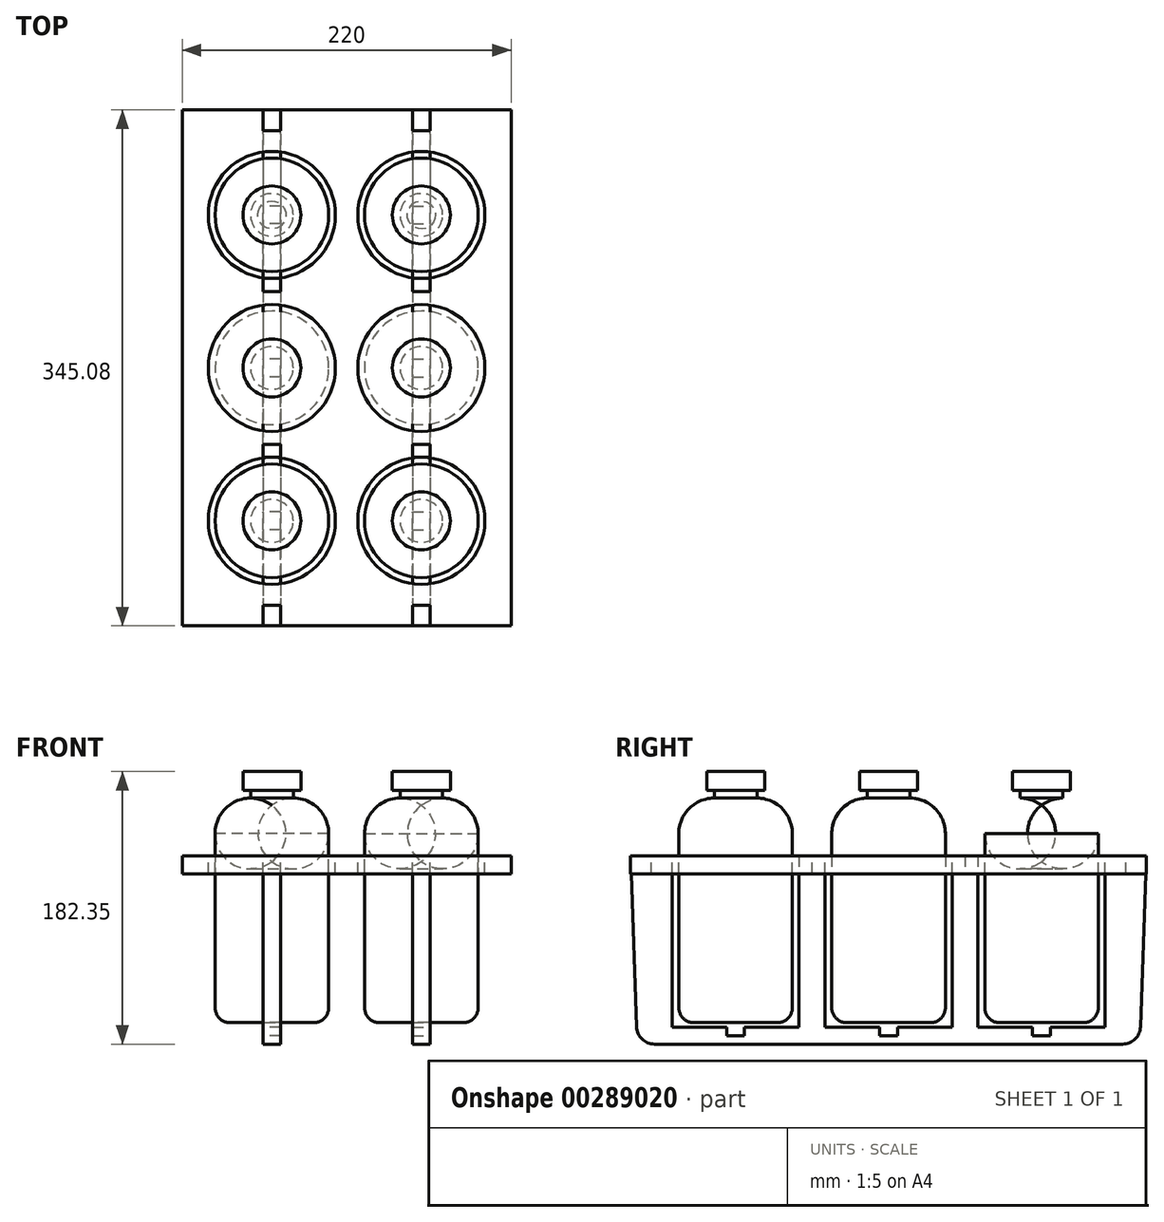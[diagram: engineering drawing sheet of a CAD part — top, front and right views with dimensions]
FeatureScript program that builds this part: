
annotation { "Feature Type Name" : "Feature", "Feature Type Description" : "" }
export const myFeature = defineFeature(function(context is Context, id is Id, definition is map)
    precondition{}
    {
        {
            var Q0;
            Q0=qCreatedBy(makeId("Right.planeOp"),FACE);
            var sketch = newSketch(context, id + "F0", { "sketchPlane" : qUnion([Q0])});
            skLineSegment(sketch, "E0", {"start": v(0, 0) * mm, "end": v(-156.67, 0) * mm});
            skLineSegment(sketch, "E1", {"start": v(-156.67, 0) * mm, "end": v(-172, 0) * mm, "construction": true});
            skLineSegment(sketch, "E2", {"start": v(-172, 0) * mm, "end": v(-172.54, 15.32) * mm, "construction": true});
            skLineSegment(sketch, "E3", {"start": v(-172.54, 15.32) * mm, "end": v(-177.14, 147.24) * mm});
            skLineSegment(sketch, "E4", {"start": v(-172, 0) * mm, "end": v(-172, 147.24) * mm, "construction": true});
            skArc(sketch, "E5", {"start": v(-172.54, 15.32) * mm, "mid": v(-167.7, 4.46) * mm, "end": v(-156.67, 0) * mm});
            skLineSegment(sketch, "E6", {"start": v(0, 0) * mm, "end": v(0, 147.24) * mm, "construction": true});
            skLineSegment(sketch, "E7.MirrorCS", {"start": v(0, 0) * mm, "end": v(156.67, 0) * mm});
            skArc(sketch, "E8.MirrorCS", {"start": v(172.54, 15.32) * mm, "mid": v(167.7, 4.46) * mm, "end": v(156.67, 0) * mm});
            skLineSegment(sketch, "E9.MirrorCS", {"start": v(172.54, 15.32) * mm, "end": v(177.14, 147.24) * mm});
            skLineSegment(sketch, "E10", {"start": v(-177.14, 147.24) * mm, "end": v(177.14, 147.24) * mm, "construction": true});
            skSolve(sketch);
        }
        {
            var Q0;
            Q0=qCreatedBy(makeId("Front.planeOp"),FACE);
            var sketch = newSketch(context, id + "F1", { "sketchPlane" : qUnion([Q0])});
            skLineSegment(sketch, "E11", {"start": v(0, 0) * mm, "end": v(-233, 0) * mm});
            skLineSegment(sketch, "E12", {"start": v(-233, 0) * mm, "end": v(-248.3, 0) * mm, "construction": true});
            skLineSegment(sketch, "E13", {"start": v(-248.3, 0) * mm, "end": v(-248.83, 15.3) * mm, "construction": true});
            skLineSegment(sketch, "E14", {"start": v(-248.83, 15.3) * mm, "end": v(-253.44, 147.24) * mm});
            skLineSegment(sketch, "E15", {"start": v(-253.44, 147.24) * mm, "end": v(0, 147.24) * mm, "construction": true});
            skArc(sketch, "E16", {"start": v(-248.83, 15.3) * mm, "mid": v(-244, 4.45) * mm, "end": v(-233, 0) * mm});
            skLineSegment(sketch, "E17", {"start": v(-248.3, 0) * mm, "end": v(-248.3, 147.24) * mm, "construction": true});
            skLineSegment(sketch, "E18", {"start": v(0, 147.24) * mm, "end": v(0, 0) * mm, "construction": true});
            skLineSegment(sketch, "E19.MirrorCS", {"start": v(0, 0) * mm, "end": v(233, 0) * mm});
            skArc(sketch, "E20.MirrorCS", {"start": v(248.83, 15.3) * mm, "mid": v(244, 4.45) * mm, "end": v(233, 0) * mm});
            skLineSegment(sketch, "E21.MirrorCS", {"start": v(248.83, 15.3) * mm, "end": v(253.44, 147.24) * mm});
            skSolve(sketch);
        }
        {
            var Q0;
            Q0=qCreatedBy(makeId("Right.planeOp"),FACE);
            cPlane(context, id + "F2", {"entities" : qUnion([Q0]), "cplaneType" : CPlaneType.OFFSET, "offset" : 50 * mm, "oppositeDirection" : true, "width" : 150 * mm, "height" : 150 * mm});
        }
        {
            var Q0;
            Q0=qCreatedBy(id+"F2.planeOp",FACE);
            cPlane(context, id + "F3", {"entities" : qUnion([Q0]), "cplaneType" : CPlaneType.OFFSET, "offset" : 100 * mm, "oppositeDirection" : true, "width" : 150 * mm, "height" : 150 * mm});
        }
        {
            var Q0;
            Q0=qCreatedBy(id+"F2.planeOp",FACE);
            var sketch = newSketch(context, id + "F4", { "sketchPlane" : qUnion([Q0])});
            skLineSegment(sketch, "E22", {"start": v(0, 0) * mm, "end": v(0, 186.35) * mm});
            skLineSegment(sketch, "E23", {"start": v(0, 18.35) * mm, "end": v(38, 18.35) * mm});
            skLineSegment(sketch, "E24", {"start": v(38, 18.35) * mm, "end": v(38, 186.35) * mm, "construction": true});
            skLineSegment(sketch, "E25", {"start": v(0, 186.35) * mm, "end": v(38, 186.35) * mm, "construction": true});
            skLineSegment(sketch, "E26", {"start": v(38, 18.35) * mm, "end": v(70.17, 18.35) * mm, "construction": true});
            skLineSegment(sketch, "E27", {"start": v(70.17, 18.35) * mm, "end": v(70.17, 173.98) * mm, "construction": true});
            skLineSegment(sketch, "E28.MirrorCS", {"start": v(140.34, 0) * mm, "end": v(140.34, 18.35) * mm});
            skLineSegment(sketch, "E29.MirrorCS", {"start": v(140.34, 18.35) * mm, "end": v(102.34, 18.35) * mm});
            skLineSegment(sketch, "E30.MirrorCS", {"start": v(-140.34, 186.35) * mm, "end": v(-102.34, 186.35) * mm, "construction": true});
            skLineSegment(sketch, "E31.MirrorCS", {"start": v(-140.34, 0) * mm, "end": v(-140.34, 186.35) * mm});
            skLineSegment(sketch, "E32.MirrorCS", {"start": v(-140.34, 18.35) * mm, "end": v(-102.34, 18.35) * mm});
            skLineSegment(sketch, "E33", {"start": v(19.39, 186.35) * mm, "end": v(19.39, 173.6) * mm});
            skLineSegment(sketch, "E34", {"start": v(19.39, 173.6) * mm, "end": v(14.28, 173.6) * mm});
            skLineSegment(sketch, "E35", {"start": v(14.28, 173.6) * mm, "end": v(14.28, 168.6) * mm});
            skLineSegment(sketch, "E36", {"start": v(38, 18.35) * mm, "end": v(38, 144.89) * mm});
            skArc(sketch, "E37", {"start": v(38, 144.89) * mm, "mid": v(31.05, 161.66) * mm, "end": v(14.28, 168.6) * mm});
            skLineSegment(sketch, "E38", {"start": v(14.28, 168.6) * mm, "end": v(0, 168.6) * mm, "construction": true});
            skLineSegment(sketch, "E39", {"start": v(19.39, 186.35) * mm, "end": v(0, 186.35) * mm});
            skLineSegment(sketch, "E40", {"start": v(102.34, 144.89) * mm, "end": v(102.34, 18.35) * mm});
            skPoint(sketch, "E41.orphan", {"position": v(140.34, 186.35) * mm});
            skPoint(sketch, "E42.MirrorCS.end.orphan", {"position": v(102.34, 186.35) * mm});
            skLineSegment(sketch, "E43", {"start": v(140.34, 144.89) * mm, "end": v(140.34, 186.35) * mm, "construction": true});
            skLineSegment(sketch, "E44", {"start": v(102.34, 186.35) * mm, "end": v(140.34, 186.35) * mm, "construction": true});
            skLineSegment(sketch, "E45", {"start": v(102.34, 186.35) * mm, "end": v(121.73, 186.35) * mm});
            skLineSegment(sketch, "E46", {"start": v(121.73, 186.35) * mm, "end": v(121.73, 173.6) * mm});
            skLineSegment(sketch, "E47", {"start": v(121.73, 173.6) * mm, "end": v(116.62, 173.6) * mm});
            skLineSegment(sketch, "E48", {"start": v(116.62, 173.6) * mm, "end": v(116.62, 168.6) * mm});
            skLineSegment(sketch, "E49", {"start": v(116.62, 168.6) * mm, "end": v(14.28, 168.6) * mm, "construction": true});
            skArc(sketch, "E50", {"start": v(140.34, 144.89) * mm, "mid": v(133.4, 161.66) * mm, "end": v(116.62, 168.6) * mm});
            skLineSegment(sketch, "E51", {"start": v(38, 144.89) * mm, "end": v(140.34, 144.89) * mm, "construction": true});
            skLineSegment(sketch, "E52", {"start": v(140.34, 144.89) * mm, "end": v(140.34, 18.35) * mm, "construction": true});
            skLineSegment(sketch, "E53", {"start": v(102.34, 144.89) * mm, "end": v(102.34, 186.35) * mm});
            skPoint(sketch, "E54.end.orphan", {"position": v(-102.34, 18.35) * mm});
            skPoint(sketch, "E55.MirrorCS.end.orphan", {"position": v(-102.34, 144.89) * mm});
            skPoint(sketch, "E55.MirrorCS.start.orphan", {"position": v(-102.34, 186.35) * mm});
            skLineSegment(sketch, "E56", {"start": v(140.34, 144.89) * mm, "end": v(140.34, 18.35) * mm});
            skLineSegment(sketch, "E57.MirrorCS", {"start": v(-140.34, 144.89) * mm, "end": v(-140.34, 18.35) * mm, "construction": true});
            skArc(sketch, "E58.MirrorCS", {"start": v(-140.34, 144.89) * mm, "mid": v(-133.4, 161.66) * mm, "end": v(-116.62, 168.6) * mm});
            skLineSegment(sketch, "E59.MirrorCS", {"start": v(-116.62, 173.6) * mm, "end": v(-116.62, 168.6) * mm});
            skLineSegment(sketch, "E60.MirrorCS", {"start": v(-121.73, 173.6) * mm, "end": v(-116.62, 173.6) * mm});
            skLineSegment(sketch, "E61.MirrorCS", {"start": v(-121.73, 186.35) * mm, "end": v(-121.73, 173.6) * mm});
            skLineSegment(sketch, "E62.MirrorCS", {"start": v(-102.34, 186.35) * mm, "end": v(-140.34, 186.35) * mm, "construction": true});
            skLineSegment(sketch, "E63.MirrorCS", {"start": v(-102.34, 144.89) * mm, "end": v(-102.34, 18.35) * mm});
            skLineSegment(sketch, "E64.MirrorCS", {"start": v(-102.34, 144.89) * mm, "end": v(-102.34, 186.35) * mm});
            skLineSegment(sketch, "E65", {"start": v(-102.34, 186.35) * mm, "end": v(-121.73, 186.35) * mm});
            skLineSegment(sketch, "E66", {"start": v(167.73, 15.34) * mm, "end": v(140.34, 15.34) * mm});
            skSolve(sketch);
        }
        {
            var Q0;
            {var subQ2=sQuery(id+"F4.wireOp",EDGE,"E23");Q0=makeQuery(id+"F4.imprint","IMPRINT",FACE,{"disambiguationData":[TD([[makeQuery(id+"F4.imprint","IMPRINT",EDGE,{"derivedFrom":subQ2}),1.0]])]});}
            var Q1;
            Q1=sQuery(id+"F4.wireOp",EDGE,"E22");
            revolve(context, id + "F5", {"entities" : qUnion([Q0]), "axis" : qUnion([Q1]), "revolveType" : RevolveType.FULL});
        }
        {
            var Q0;
            {var subQ1=sQuery(id+"F4.wireOp",EDGE,"E32.MirrorCS");Q0=makeQuery(id+"F4.imprint","IMPRINT",FACE,{"disambiguationData":[TD([[makeQuery(id+"F4.imprint","IMPRINT",EDGE,{"derivedFrom":subQ1}),1.0]])]});}
            var Q1;
            Q1=sQuery(id+"F4.wireOp",EDGE,"E63.MirrorCS");
            revolve(context, id + "F6", {"entities" : qUnion([Q0]), "axis" : qUnion([Q1]), "revolveType" : RevolveType.FULL});
        }
        {
            var Q0;
            Q0=makeQuery(id+"F4.imprint","IMPRINT",FACE,{"disambiguationData":[TD([[makeQuery(id+"F4.imprint","IMPRINT",EDGE,{"derivedFrom":sQuery(id+"F4.wireOp",EDGE,"E29.MirrorCS")}),-1.0]])]});
            var Q1;
            Q1=sQuery(id+"F4.wireOp",EDGE,"E40");
            revolve(context, id + "F7", {"entities" : qUnion([Q0]), "axis" : qUnion([Q1]), "revolveType" : RevolveType.FULL});
        }
        {
            var Q0;
            Q0=makeQuery(id+"F7.opRevolve","SWEPT_EDGE",EDGE,{"disambiguationData":[OSD([sQuery(id+"F4.wireOp",EDGE,"E29.MirrorCS"),sQuery(id+"F4.wireOp",EDGE,"E56")])]});
            var Q1;
            Q1=makeQuery(id+"F5.opRevolve","SWEPT_EDGE",EDGE,{"disambiguationData":[OSD([sQuery(id+"F4.wireOp",EDGE,"E23"),sQuery(id+"F4.wireOp",EDGE,"E36")])]});
            var Q2;
            Q2=makeQuery(id+"F6.opRevolve","SWEPT_EDGE",EDGE,{"disambiguationData":[OSD([sQuery(id+"F4.wireOp",EDGE,"E31.MirrorCS"),sQuery(id+"F4.wireOp",EDGE,"E32.MirrorCS")])]});
            fillet(context, id + "F8", {"entities" : qUnion([Q0, Q1, Q2]), "radius" : 10 * mm, "tangentPropagation" : true, "allowEdgeOverflow" : false});
        }
        {
            var Q0;
            Q0=makeQuery(id+"F7.opRevolve","SWEPT_BODY",BODY,{"disambiguationData":[OSD([sQuery(id+"F4.wireOp",EDGE,"E29.MirrorCS"),sQuery(id+"F4.wireOp",EDGE,"E40"),sQuery(id+"F4.wireOp",EDGE,"E45"),sQuery(id+"F4.wireOp",EDGE,"E46"),sQuery(id+"F4.wireOp",EDGE,"E47"),sQuery(id+"F4.wireOp",EDGE,"E48"),sQuery(id+"F4.wireOp",EDGE,"E50"),sQuery(id+"F4.wireOp",EDGE,"E53"),sQuery(id+"F4.wireOp",EDGE,"E56")])]});
            var Q1;
            Q1=makeQuery(id+"F5.opRevolve","SWEPT_BODY",BODY,{"disambiguationData":[OSD([sQuery(id+"F4.wireOp",EDGE,"E22"),sQuery(id+"F4.wireOp",EDGE,"E23"),sQuery(id+"F4.wireOp",EDGE,"E33"),sQuery(id+"F4.wireOp",EDGE,"E34"),sQuery(id+"F4.wireOp",EDGE,"E35"),sQuery(id+"F4.wireOp",EDGE,"E36"),sQuery(id+"F4.wireOp",EDGE,"E37"),sQuery(id+"F4.wireOp",EDGE,"E39")])]});
            var Q2;
            Q2=makeQuery(id+"F6.opRevolve","SWEPT_BODY",BODY,{"disambiguationData":[OSD([sQuery(id+"F4.wireOp",EDGE,"E31.MirrorCS"),sQuery(id+"F4.wireOp",EDGE,"E32.MirrorCS"),sQuery(id+"F4.wireOp",EDGE,"E58.MirrorCS"),sQuery(id+"F4.wireOp",EDGE,"E59.MirrorCS"),sQuery(id+"F4.wireOp",EDGE,"E60.MirrorCS"),sQuery(id+"F4.wireOp",EDGE,"E61.MirrorCS"),sQuery(id+"F4.wireOp",EDGE,"E63.MirrorCS"),sQuery(id+"F4.wireOp",EDGE,"E64.MirrorCS"),sQuery(id+"F4.wireOp",EDGE,"E65")])]});
            var Q3;
            Q3=qCreatedBy(makeId("Right.planeOp"),FACE);
            mirror(context, id + "F9", {"entities" : qUnion([Q0, Q1, Q2]), "mirrorPlane" : qUnion([Q3])});
        }
        {
            var Q0;
            Q0=qCreatedBy(makeId("Top.planeOp"),FACE);
            cPlane(context, id + "F10", {"entities" : qUnion([Q0]), "cplaneType" : CPlaneType.OFFSET, "offset" : 130 * mm, "width" : 150 * mm, "height" : 150 * mm});
        }
        {
            var Q0;
            Q0=qCreatedBy(id+"F10.planeOp",FACE);
            var sketch = newSketch(context, id + "F11", { "sketchPlane" : qUnion([Q0])});
            skCircle(sketch, "E67", {"center": v(-50, 0) * mm, "radius": 42.5 * mm});
            skCircle(sketch, "E68", {"center": v(-50, 102.34) * mm, "radius": 42.5 * mm});
            skCircle(sketch, "E69", {"center": v(-50, -102.34) * mm, "radius": 42.5 * mm});
            skLineSegment(sketch, "E70", {"start": v(0, 0) * mm, "end": v(0, -172.54) * mm, "construction": true});
            skLineSegment(sketch, "E71", {"start": v(0, -172.54) * mm, "end": v(-110, -172.54) * mm});
            skLineSegment(sketch, "E72", {"start": v(-110, -172.54) * mm, "end": v(-110, 0) * mm});
            skLineSegment(sketch, "E73", {"start": v(-110, 0) * mm, "end": v(0, 0) * mm, "construction": true});
            skLineSegment(sketch, "E74.MirrorCS", {"start": v(-110, 172.54) * mm, "end": v(-110, 0) * mm});
            skLineSegment(sketch, "E75.MirrorCS", {"start": v(0, 172.54) * mm, "end": v(-110, 172.54) * mm});
            skLineSegment(sketch, "E76.MirrorCS", {"start": v(0, -172.54) * mm, "end": v(110, -172.54) * mm});
            skLineSegment(sketch, "E77.MirrorCS", {"start": v(110, -172.54) * mm, "end": v(110, 0) * mm});
            skLineSegment(sketch, "E78.MirrorCS", {"start": v(0, 172.54) * mm, "end": v(110, 172.54) * mm});
            skLineSegment(sketch, "E79.MirrorCS", {"start": v(110, 172.54) * mm, "end": v(110, 0) * mm});
            skCircle(sketch, "E80.MirrorC", {"center": v(50, 0) * mm, "radius": 42.5 * mm});
            skCircle(sketch, "E81.MirrorC", {"center": v(50, -102.34) * mm, "radius": 42.5 * mm});
            skCircle(sketch, "E82.MirrorC", {"center": v(50, 102.34) * mm, "radius": 42.5 * mm});
            skLineSegment(sketch, "E83", {"start": v(0, 172.54) * mm, "end": v(0, 176.54) * mm});
            skSolve(sketch);
        }
        {
            var Q0;
            Q0=makeQuery(id+"F11.imprint","IMPRINT",FACE,{"disambiguationData":[TD([[makeQuery(id+"F11.imprint","IMPRINT",EDGE,{"derivedFrom":sQuery(id+"F11.wireOp",EDGE,"E67")}),-1.0]])]});
            extrude(context, id + "F12", {"entities" : qUnion([Q0]), "oppositeDirection" : true, "depth" : 12 * mm});
        }
        {
            var Q0;
            Q0=qCreatedBy(id+"F2.planeOp",FACE);
            var sketch = newSketch(context, id + "F13", { "sketchPlane" : qUnion([Q0])});
            skLineSegment(sketch, "E84", {"start": v(172.54, 130) * mm, "end": v(168.54, 15.6) * mm});
            skLineSegment(sketch, "E85", {"start": v(156.53, 4) * mm, "end": v(0, 4) * mm});
            skArc(sketch, "E86", {"start": v(156.53, 4) * mm, "mid": v(164.88, 7.37) * mm, "end": v(168.54, 15.6) * mm});
            skLineSegment(sketch, "E87", {"start": v(59.84, 130) * mm, "end": v(42.5, 130) * mm, "construction": true});
            skLineSegment(sketch, "E88", {"start": v(51.17, 130) * mm, "end": v(51.17, 4) * mm, "construction": true});
            skLineSegment(sketch, "E89", {"start": v(51.17, 130) * mm, "end": v(59.84, 130) * mm});
            skLineSegment(sketch, "E90", {"start": v(59.84, 130) * mm, "end": v(59.84, 15.43) * mm});
            skLineSegment(sketch, "E91", {"start": v(59.84, 15.43) * mm, "end": v(102.34, 15.43) * mm});
            skLineSegment(sketch, "E92", {"start": v(59.84, 130) * mm, "end": v(144.84, 130) * mm, "construction": true});
            skLineSegment(sketch, "E93", {"start": v(102.34, 130) * mm, "end": v(102.34, 15.43) * mm, "construction": true});
            skLineSegment(sketch, "E94.MirrorCS", {"start": v(144.84, 15.43) * mm, "end": v(102.34, 15.43) * mm});
            skLineSegment(sketch, "E95.MirrorCS", {"start": v(144.84, 130) * mm, "end": v(144.84, 15.43) * mm, "construction": true});
            skLineSegment(sketch, "E96", {"start": v(144.84, 15.43) * mm, "end": v(144.84, 118) * mm, "construction": true});
            skLineSegment(sketch, "E97", {"start": v(144.84, 118) * mm, "end": v(158.7, 118) * mm});
            skLineSegment(sketch, "E98", {"start": v(158.7, 118) * mm, "end": v(158.7, 130) * mm});
            skLineSegment(sketch, "E99", {"start": v(158.7, 130) * mm, "end": v(172.54, 130) * mm});
            skLineSegment(sketch, "E100", {"start": v(144.84, 118) * mm, "end": v(144.84, 15.43) * mm});
            skLineSegment(sketch, "E101", {"start": v(51.17, 130) * mm, "end": v(51.17, 118) * mm});
            skLineSegment(sketch, "E102", {"start": v(51.17, 118) * mm, "end": v(42.5, 118) * mm});
            skLineSegment(sketch, "E103", {"start": v(42.5, 118) * mm, "end": v(42.5, 15.43) * mm});
            skLineSegment(sketch, "E104", {"start": v(42.5, 15.43) * mm, "end": v(0, 15.43) * mm});
            skLineSegment(sketch, "E105", {"start": v(42.5, 15.43) * mm, "end": v(59.84, 15.43) * mm, "construction": true});
            skLineSegment(sketch, "E106", {"start": v(0, 15.43) * mm, "end": v(0, 4) * mm, "construction": true});
            skLineSegment(sketch, "E107.MirrorCS", {"start": v(-42.5, 15.43) * mm, "end": v(0, 15.43) * mm});
            skLineSegment(sketch, "E108.MirrorCS", {"start": v(-42.5, 118) * mm, "end": v(-42.5, 15.43) * mm});
            skLineSegment(sketch, "E109.MirrorCS", {"start": v(-51.17, 118) * mm, "end": v(-42.5, 118) * mm});
            skLineSegment(sketch, "E110.MirrorCS", {"start": v(-51.17, 130) * mm, "end": v(-51.17, 4) * mm, "construction": true});
            skLineSegment(sketch, "E111.MirrorCS", {"start": v(-59.84, 130) * mm, "end": v(-42.5, 130) * mm, "construction": true});
            skLineSegment(sketch, "E112.MirrorCS", {"start": v(-59.84, 130) * mm, "end": v(-59.84, 15.43) * mm});
            skLineSegment(sketch, "E113.MirrorCS", {"start": v(-59.84, 15.43) * mm, "end": v(-102.34, 15.43) * mm});
            skLineSegment(sketch, "E114.MirrorCS", {"start": v(-144.84, 15.43) * mm, "end": v(-102.34, 15.43) * mm});
            skLineSegment(sketch, "E115.MirrorCS", {"start": v(-144.84, 15.43) * mm, "end": v(-144.84, 118) * mm, "construction": true});
            skLineSegment(sketch, "E116.MirrorCS", {"start": v(-144.84, 118) * mm, "end": v(-158.7, 118) * mm});
            skLineSegment(sketch, "E117.MirrorCS", {"start": v(-158.7, 118) * mm, "end": v(-158.7, 130) * mm});
            skLineSegment(sketch, "E118.MirrorCS", {"start": v(-158.7, 130) * mm, "end": v(-172.54, 130) * mm});
            skLineSegment(sketch, "E119.MirrorCS", {"start": v(-172.54, 130) * mm, "end": v(-168.54, 15.6) * mm});
            skArc(sketch, "E120.MirrorCS", {"start": v(-156.53, 4) * mm, "mid": v(-164.88, 7.37) * mm, "end": v(-168.54, 15.6) * mm});
            skLineSegment(sketch, "E121.MirrorCS", {"start": v(-156.53, 4) * mm, "end": v(0, 4) * mm});
            skLineSegment(sketch, "E122", {"start": v(-51.17, 118) * mm, "end": v(-51.17, 130) * mm});
            skLineSegment(sketch, "E123", {"start": v(-51.17, 130) * mm, "end": v(-59.84, 130) * mm});
            skLineSegment(sketch, "E124", {"start": v(-144.84, 118) * mm, "end": v(-144.84, 15.43) * mm});
            skLineSegment(sketch, "E125", {"start": v(102.34, 15.43) * mm, "end": v(102.34, 4) * mm});
            skLineSegment(sketch, "E126", {"start": v(102.34, 9.71) * mm, "end": v(108.34, 9.71) * mm});
            skLineSegment(sketch, "E127", {"start": v(108.34, 9.71) * mm, "end": v(108.34, 15.43) * mm});
            skLineSegment(sketch, "E128.MirrorCS", {"start": v(102.34, 9.71) * mm, "end": v(96.34, 9.71) * mm});
            skLineSegment(sketch, "E129.MirrorCS", {"start": v(96.34, 9.71) * mm, "end": v(96.34, 15.43) * mm});
            skLineSegment(sketch, "E130.MirrorCS", {"start": v(6, 9.71) * mm, "end": v(6, 15.43) * mm});
            skLineSegment(sketch, "E131.MirrorCS", {"start": v(0, 9.71) * mm, "end": v(6, 9.71) * mm});
            skLineSegment(sketch, "E132.MirrorCS", {"start": v(0, 9.71) * mm, "end": v(-6, 9.71) * mm});
            skLineSegment(sketch, "E133.MirrorCS", {"start": v(-6, 9.71) * mm, "end": v(-6, 15.43) * mm});
            skLineSegment(sketch, "E134.MirrorCS", {"start": v(102.34, 15.43) * mm, "end": v(102.34, 4) * mm, "construction": true});
            skLineSegment(sketch, "E135.MirrorCS", {"start": v(-96.34, 9.71) * mm, "end": v(-96.34, 15.43) * mm});
            skLineSegment(sketch, "E136.MirrorCS", {"start": v(-102.34, 9.71) * mm, "end": v(-96.34, 9.71) * mm});
            skLineSegment(sketch, "E137.MirrorCS", {"start": v(-102.34, 9.71) * mm, "end": v(-108.34, 9.71) * mm});
            skLineSegment(sketch, "E138.MirrorCS", {"start": v(-108.34, 9.71) * mm, "end": v(-108.34, 15.43) * mm});
            skSolve(sketch);
        }
        {
            var Q0;
            Q0=makeQuery(id+"F13.imprint","IMPRINT",FACE,{"disambiguationData":[TD([[makeQuery(id+"F13.imprint","IMPRINT",EDGE,{"derivedFrom":sQuery(id+"F13.wireOp",EDGE,"E84")}),-1.0]])]});
            var Q1;
            Q1=makeQuery(id+"F13.imprint","IMPRINT",FACE,{"disambiguationData":[TD([[makeQuery(id+"F13.imprint","IMPRINT",EDGE,{"derivedFrom":sQuery(id+"F13.wireOp",EDGE,"E89")}),-1.0]])]});
            extrude(context, id + "F14", {"entities" : qUnion([Q0, Q1]), "endBound" : BoundingType.SYMMETRIC, "depth" : 12 * mm});
        }
        {
            var Q0;
            Q0=makeQuery(id+"F14.opExtrude","SWEPT_BODY",BODY,{"disambiguationData":[OSD([sQuery(id+"F13.wireOp",EDGE,"E84"),sQuery(id+"F13.wireOp",EDGE,"E85"),sQuery(id+"F13.wireOp",EDGE,"E86"),sQuery(id+"F13.wireOp",EDGE,"E89"),sQuery(id+"F13.wireOp",EDGE,"E90"),sQuery(id+"F13.wireOp",EDGE,"E91"),sQuery(id+"F13.wireOp",EDGE,"E94.MirrorCS"),sQuery(id+"F13.wireOp",EDGE,"E97"),sQuery(id+"F13.wireOp",EDGE,"E98"),sQuery(id+"F13.wireOp",EDGE,"E99"),sQuery(id+"F13.wireOp",EDGE,"E100"),sQuery(id+"F13.wireOp",EDGE,"E101"),sQuery(id+"F13.wireOp",EDGE,"E102"),sQuery(id+"F13.wireOp",EDGE,"E103"),sQuery(id+"F13.wireOp",EDGE,"E104"),sQuery(id+"F13.wireOp",EDGE,"E107.MirrorCS"),sQuery(id+"F13.wireOp",EDGE,"E108.MirrorCS"),sQuery(id+"F13.wireOp",EDGE,"E109.MirrorCS"),sQuery(id+"F13.wireOp",EDGE,"E112.MirrorCS"),sQuery(id+"F13.wireOp",EDGE,"E113.MirrorCS"),sQuery(id+"F13.wireOp",EDGE,"E114.MirrorCS"),sQuery(id+"F13.wireOp",EDGE,"E116.MirrorCS"),sQuery(id+"F13.wireOp",EDGE,"E117.MirrorCS"),sQuery(id+"F13.wireOp",EDGE,"E118.MirrorCS"),sQuery(id+"F13.wireOp",EDGE,"E119.MirrorCS"),sQuery(id+"F13.wireOp",EDGE,"E120.MirrorCS"),sQuery(id+"F13.wireOp",EDGE,"E121.MirrorCS"),sQuery(id+"F13.wireOp",EDGE,"E122"),sQuery(id+"F13.wireOp",EDGE,"E123"),sQuery(id+"F13.wireOp",EDGE,"E124"),sQuery(id+"F13.wireOp",EDGE,"E126"),sQuery(id+"F13.wireOp",EDGE,"E127"),sQuery(id+"F13.wireOp",EDGE,"E128.MirrorCS"),sQuery(id+"F13.wireOp",EDGE,"E129.MirrorCS"),sQuery(id+"F13.wireOp",EDGE,"E130.MirrorCS"),sQuery(id+"F13.wireOp",EDGE,"E131.MirrorCS"),sQuery(id+"F13.wireOp",EDGE,"E132.MirrorCS"),sQuery(id+"F13.wireOp",EDGE,"E133.MirrorCS"),sQuery(id+"F13.wireOp",EDGE,"E135.MirrorCS"),sQuery(id+"F13.wireOp",EDGE,"E136.MirrorCS"),sQuery(id+"F13.wireOp",EDGE,"E137.MirrorCS"),sQuery(id+"F13.wireOp",EDGE,"E138.MirrorCS")])]});
            var Q1;
            Q1=qCreatedBy(makeId("Right.planeOp"),FACE);
            mirror(context, id + "F15", {"entities" : qUnion([Q0]), "mirrorPlane" : qUnion([Q1])});
        }
    });
